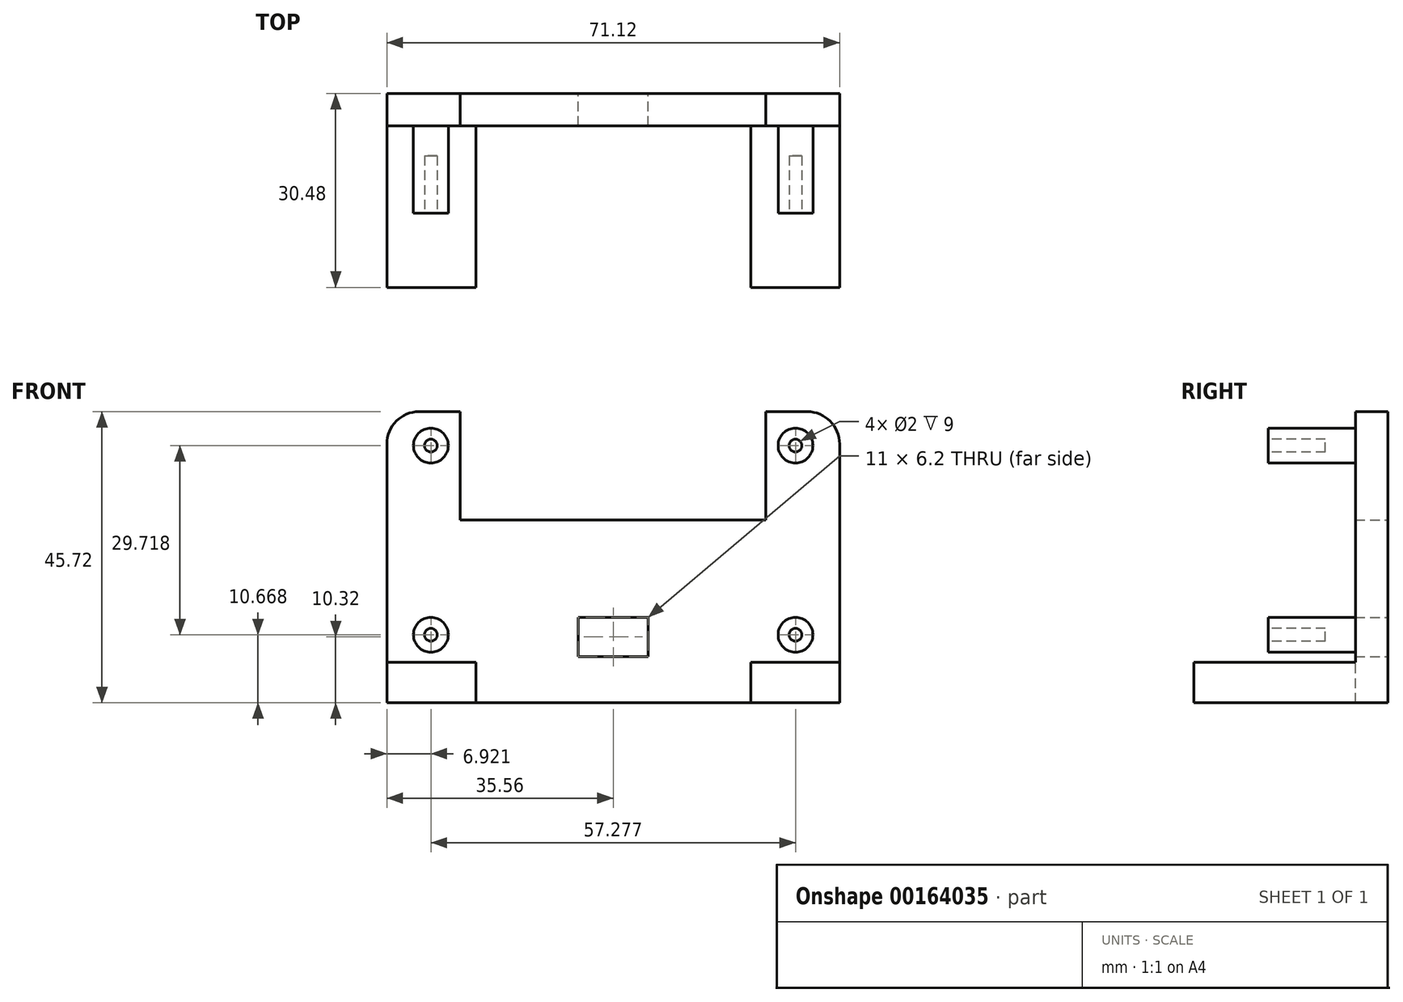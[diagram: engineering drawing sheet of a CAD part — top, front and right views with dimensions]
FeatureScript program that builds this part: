
annotation { "Feature Type Name" : "Feature", "Feature Type Description" : "" }
export const myFeature = defineFeature(function(context is Context, id is Id, definition is map)
    precondition{}
    {
        {
            var Q0;
            Q0=qCreatedBy(makeId("Front.planeOp"),FACE);
            var sketch = newSketch(context, id + "F0", { "sketchPlane" : qUnion([Q0])});
            skLineSegment(sketch, "E0.bottom", {"start": v(0, 0) * mm, "end": v(71.12, 0) * mm});
            skLineSegment(sketch, "E0.top", {"start": v(0, 45.72) * mm, "end": v(71.12, 45.72) * mm});
            skLineSegment(sketch, "E0.left", {"start": v(0, 0) * mm, "end": v(0, 45.72) * mm});
            skLineSegment(sketch, "E0.right", {"start": v(71.12, 0) * mm, "end": v(71.12, 45.72) * mm});
            skLineSegment(sketch, "E1", {"start": v(6.92, 45.72) * mm, "end": v(6.92, 0) * mm, "construction": true});
            skLineSegment(sketch, "E2", {"start": v(64.2, 45.72) * mm, "end": v(64.2, 0) * mm, "construction": true});
            skLineSegment(sketch, "E3", {"start": v(0, 40.39) * mm, "end": v(71.12, 40.39) * mm, "construction": true});
            skCircle(sketch, "E4", {"center": v(6.92, 40.39) * mm, "radius": 2.73 * mm});
            skCircle(sketch, "E5", {"center": v(64.2, 40.39) * mm, "radius": 2.73 * mm});
            skCircle(sketch, "E6", {"center": v(6.92, 10.67) * mm, "radius": 2.73 * mm});
            skCircle(sketch, "E7", {"center": v(64.2, 10.67) * mm, "radius": 2.73 * mm});
            skLineSegment(sketch, "E8", {"start": v(35.56, 45.72) * mm, "end": v(35.56, 0) * mm, "construction": true});
            skLineSegment(sketch, "E9.bottom", {"start": v(0, 6.35) * mm, "end": v(71.12, 6.35) * mm});
            skLineSegment(sketch, "E9.left", {"start": v(0, 6.35) * mm, "end": v(0, 0) * mm});
            skLineSegment(sketch, "E9.right", {"start": v(71.12, 6.35) * mm, "end": v(71.12, 0) * mm});
            skSolve(sketch);
        }
        {
            var Q0;
            Q0=makeQuery(id+"F0.imprint","IMPRINT",FACE,{"disambiguationData":[TD([[makeQuery(id+"F0.imprint","IMPRINT",EDGE,{"derivedFrom":sQuery(id+"F0.wireOp",EDGE,"E4")}),1.0]])]});
            var Q1;
            Q1=makeQuery(id+"F0.imprint","IMPRINT",FACE,{"disambiguationData":[TD([[makeQuery(id+"F0.imprint","IMPRINT",EDGE,{"derivedFrom":sQuery(id+"F0.wireOp",EDGE,"E6")}),1.0]])]});
            var Q2;
            Q2=makeQuery(id+"F0.imprint","IMPRINT",FACE,{"disambiguationData":[TD([[makeQuery(id+"F0.imprint","IMPRINT",EDGE,{"derivedFrom":sQuery(id+"F0.wireOp",EDGE,"E7")}),1.0]])]});
            var Q3;
            Q3=makeQuery(id+"F0.imprint","IMPRINT",FACE,{"disambiguationData":[TD([[makeQuery(id+"F0.imprint","IMPRINT",EDGE,{"derivedFrom":sQuery(id+"F0.wireOp",EDGE,"E5")}),1.0]])]});
            extrude(context, id + "F1", {"entities" : qUnion([Q0, Q1, Q2, Q3]), "depth" : 13.72 * mm});
        }
        {
            var Q0;
            Q0=makeQuery(id+"F0.imprint","IMPRINT",FACE,{"disambiguationData":[TD([[makeQuery(id+"F0.imprint","IMPRINT",EDGE,{"derivedFrom":sQuery(id+"F0.wireOp",EDGE,"E5")}),1.0]])]});
            var Q1;
            Q1=makeQuery(id+"F0.imprint","IMPRINT",FACE,{"disambiguationData":[TD([[makeQuery(id+"F0.imprint","IMPRINT",EDGE,{"derivedFrom":sQuery(id+"F0.wireOp",EDGE,"E4")}),1.0]])]});
            var Q2;
            Q2=makeQuery(id+"F0.imprint","IMPRINT",FACE,{"disambiguationData":[TD([[makeQuery(id+"F0.imprint","IMPRINT",EDGE,{"derivedFrom":sQuery(id+"F0.wireOp",EDGE,"E6")}),1.0]])]});
            var Q3;
            Q3=makeQuery(id+"F0.imprint","IMPRINT",FACE,{"disambiguationData":[TD([[makeQuery(id+"F0.imprint","IMPRINT",EDGE,{"derivedFrom":sQuery(id+"F0.wireOp",EDGE,"E7")}),1.0]])]});
            var Q4;
            Q4=makeQuery(id+"F0.imprint","IMPRINT",FACE,{"disambiguationData":[TD([[makeQuery(id+"F0.imprint","IMPRINT",EDGE,{"derivedFrom":sQuery(id+"F0.wireOp",EDGE,"E9.bottom")}),-1.0]])]});
            var Q5;
            Q5=makeQuery(id+"F0.imprint","IMPRINT",FACE,{"disambiguationData":[TD([[makeQuery(id+"F0.imprint","IMPRINT",EDGE,{"derivedFrom":sQuery(id+"F0.wireOp",EDGE,"E0.top")}),-1.0]])]});
            extrude(context, id + "F2", {"entities" : qUnion([Q0, Q1, Q2, Q3, Q4, Q5]), "oppositeDirection" : true, "depth" : 5.08 * mm});
        }
        {
            var Q0;
            Q0=makeQuery(id+"F0.imprint","IMPRINT",FACE,{"disambiguationData":[TD([[makeQuery(id+"F0.imprint","IMPRINT",EDGE,{"derivedFrom":sQuery(id+"F0.wireOp",EDGE,"E9.bottom")}),-1.0]])]});
            extrude(context, id + "F3", {"entities" : qUnion([Q0]), "operationType" : NewBodyOperationType.ADD, "depth" : 25.4 * mm});
        }
        {
            var Q0;
            Q0=makeQuery(id+"F3.opExtrude","SWEPT_FACE",FACE,{"disambiguationData":[OSD([sQuery(id+"F0.wireOp",EDGE,"E9.bottom")])]});
            var sketch = newSketch(context, id + "F4", { "sketchPlane" : qUnion([Q0])});
            skLineSegment(sketch, "E10", {"start": v(35.56, 0) * mm, "end": v(35.56, -25.4) * mm, "construction": true});
            skLineSegment(sketch, "E11.bottom", {"start": v(13.97, 0) * mm, "end": v(57.15, 0) * mm});
            skLineSegment(sketch, "E11.top", {"start": v(13.97, -25.4) * mm, "end": v(57.15, -25.4) * mm});
            skLineSegment(sketch, "E11.left", {"start": v(13.97, 0) * mm, "end": v(13.97, -25.4) * mm});
            skLineSegment(sketch, "E11.right", {"start": v(57.15, 0) * mm, "end": v(57.15, -25.4) * mm});
            skPoint(sketch, "E11.middle", {"position": v(35.56, -12.7) * mm});
            skSolve(sketch);
        }
        {
            var Q0;
            Q0 = qSketchRegion(id + "F4", true);
            extrude(context, id + "F5", {"entities" : qUnion([Q0]), "operationType" : NewBodyOperationType.REMOVE, "endBound" : BoundingType.THROUGH_ALL, "oppositeDirection" : true, "depth" : 25.4 * mm});
        }
        {
            var Q0;
            Q0=makeQuery(id+"F1.opExtrude","CAP_FACE",FACE,{"disambiguationData":[OSD([sQuery(id+"F0.wireOp",EDGE,"E6")])],"isStart":false});
            var sketch = newSketch(context, id + "F6", { "sketchPlane" : qUnion([Q0])});
            skCircle(sketch, "E12", {"center": v(6.92, 10.67) * mm, "radius": 1 * mm});
            skCircle(sketch, "E13", {"center": v(6.92, 40.39) * mm, "radius": 1 * mm});
            skCircle(sketch, "E14", {"center": v(64.2, 40.39) * mm, "radius": 1 * mm});
            skCircle(sketch, "E15", {"center": v(64.2, 10.67) * mm, "radius": 1 * mm});
            skSolve(sketch);
        }
        {
            var Q0;
            Q0 = qSketchRegion(id + "F6", true);
            extrude(context, id + "F7", {"entities" : qUnion([Q0]), "operationType" : NewBodyOperationType.REMOVE, "oppositeDirection" : true, "depth" : 9 * mm});
        }
        {
            var Q0;
            Q0=makeQuery(id+"F2.opExtrude","SWEPT_EDGE",EDGE,{"disambiguationData":[OSD([sQuery(id+"F0.wireOp",EDGE,"E0.top"),sQuery(id+"F0.wireOp",EDGE,"E0.left")])]});
            var Q1;
            Q1=makeQuery(id+"F2.opExtrude","SWEPT_EDGE",EDGE,{"disambiguationData":[OSD([sQuery(id+"F0.wireOp",EDGE,"E0.top"),sQuery(id+"F0.wireOp",EDGE,"E0.right")])]});
            fillet(context, id + "F8", {"entities" : qUnion([Q0, Q1]), "radius" : 5.08 * mm, "tangentPropagation" : true, "allowEdgeOverflow" : false});
        }
        {
            var Q0;
            Q0=makeQuery(id+"F2.opExtrude","CAP_FACE",FACE,{"disambiguationData":[OSD([sQuery(id+"F0.wireOp",EDGE,"E0.top"),sQuery(id+"F0.wireOp",EDGE,"E0.left"),sQuery(id+"F0.wireOp",EDGE,"E0.right"),sQuery(id+"F0.wireOp",EDGE,"E0.bottom"),sQuery(id+"F0.wireOp",EDGE,"E9.left"),sQuery(id+"F0.wireOp",EDGE,"E9.right")])],"isStart":false});
            var sketch = newSketch(context, id + "F9", { "sketchPlane" : qUnion([Q0])});
            skLineSegment(sketch, "E16.bottom", {"start": v(-59.56, 45.72) * mm, "end": v(-11.56, 45.72) * mm});
            skLineSegment(sketch, "E16.top", {"start": v(-59.56, 28.72) * mm, "end": v(-11.56, 28.72) * mm});
            skLineSegment(sketch, "E16.left", {"start": v(-59.56, 45.72) * mm, "end": v(-59.56, 28.72) * mm});
            skLineSegment(sketch, "E16.right", {"start": v(-11.56, 45.72) * mm, "end": v(-11.56, 28.72) * mm});
            skLineSegment(sketch, "E17.bottom", {"start": v(-41.06, 7.22) * mm, "end": v(-30.06, 7.22) * mm});
            skLineSegment(sketch, "E17.top", {"start": v(-41.06, 13.42) * mm, "end": v(-30.06, 13.42) * mm});
            skLineSegment(sketch, "E17.left", {"start": v(-41.06, 7.22) * mm, "end": v(-41.06, 13.42) * mm});
            skLineSegment(sketch, "E17.right", {"start": v(-30.06, 7.22) * mm, "end": v(-30.06, 13.42) * mm});
            skLineSegment(sketch, "E18", {"start": v(-71.12, 34.36) * mm, "end": v(-71.12, 15.28) * mm});
            skSolve(sketch);
        }
        {
            var Q0;
            Q0 = qSketchRegion(id + "F9", true);
            extrude(context, id + "F10", {"entities" : qUnion([Q0]), "operationType" : NewBodyOperationType.REMOVE, "oppositeDirection" : true, "depth" : 25.4 * mm});
        }
    });
